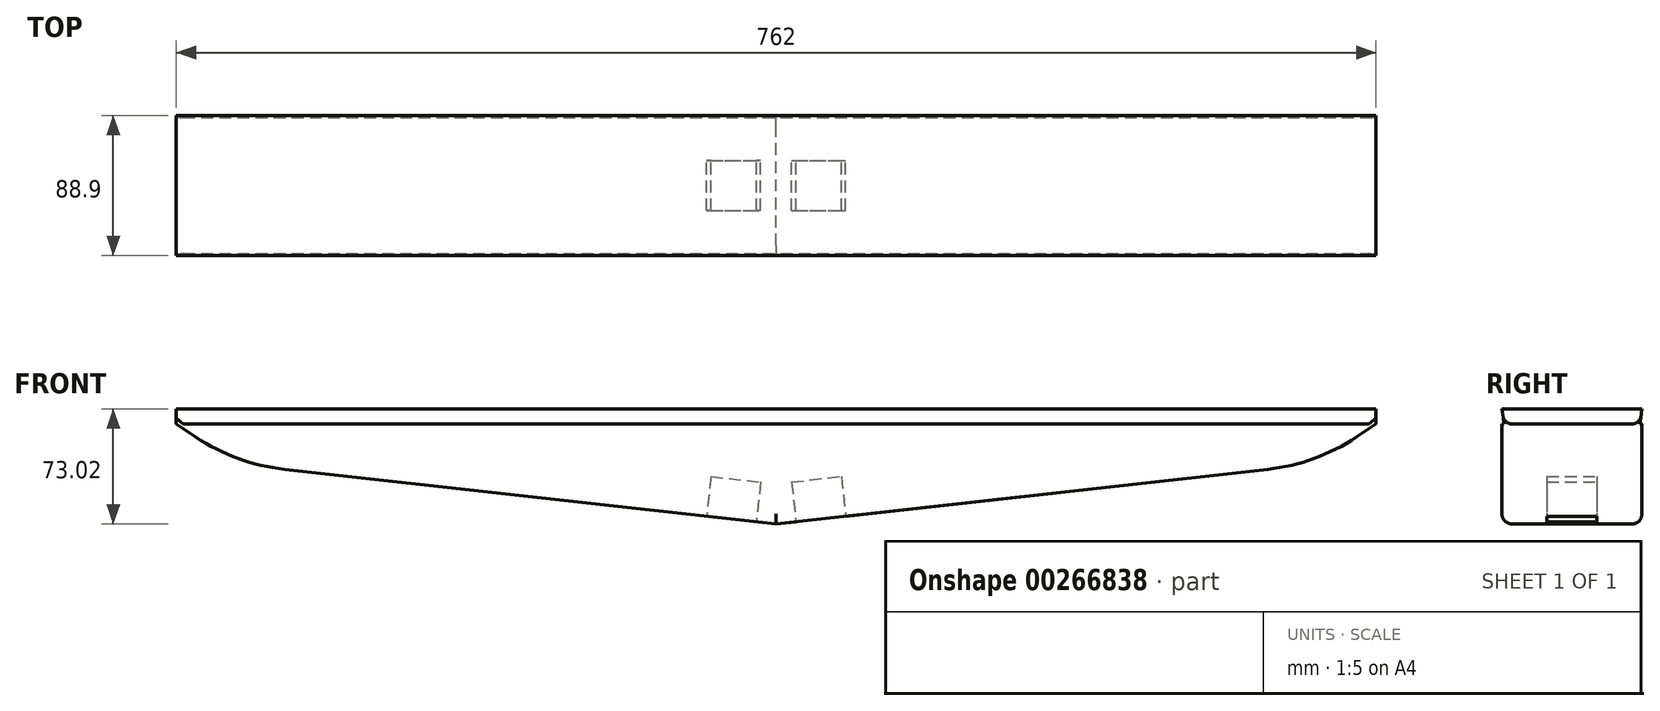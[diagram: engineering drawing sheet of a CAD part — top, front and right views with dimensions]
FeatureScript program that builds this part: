
annotation { "Feature Type Name" : "Feature", "Feature Type Description" : "" }
export const myFeature = defineFeature(function(context is Context, id is Id, definition is map)
    precondition{}
    {
        {
            var Q0;
            Q0=qCreatedBy(makeId("Front.planeOp"),FACE);
            var sketch = newSketch(context, id + "F0", { "sketchPlane" : qUnion([Q0])});
            skLineSegment(sketch, "E0", {"start": v(-380.27, 108.93) * mm, "end": v(381.73, 108.93) * mm});
            skLineSegment(sketch, "E1", {"start": v(312.91, 80.12) * mm, "end": v(0.73, 45.43) * mm});
            skLineSegment(sketch, "E2", {"start": v(0.73, 45.43) * mm, "end": v(-311.46, 80.12) * mm});
            skLineSegment(sketch, "E3", {"start": v(-367.88, 100.67) * mm, "end": v(-380.27, 108.93) * mm});
            skPoint(sketch, "E4", {"position": v(343.63, 83.53) * mm});
            skPoint(sketch, "E5.orphan", {"position": v(381.73, 87.76) * mm});
            skLineSegment(sketch, "E6", {"start": v(381.73, 108.93) * mm, "end": v(369.34, 100.67) * mm});
            skLineSegment(sketch, "E7.top", {"start": v(-380.27, 118.45) * mm, "end": v(381.73, 118.45) * mm});
            skLineSegment(sketch, "E7.left", {"start": v(-380.27, 108.93) * mm, "end": v(-380.27, 118.45) * mm});
            skLineSegment(sketch, "E7.right", {"start": v(381.73, 108.93) * mm, "end": v(381.73, 118.45) * mm});
            skLineSegment(sketch, "E8", {"start": v(31.55, 48.85) * mm, "end": v(35.36, 14.56) * mm});
            skPoint(sketch, "E9.visualSharp", {"position": v(-342.17, 83.53) * mm});
            skArc(sketch, "E9.filletArc", {"start": v(-367.88, 100.67) * mm, "mid": v(-340.9, 87.01) * mm, "end": v(-311.46, 80.12) * mm});
            skArc(sketch, "E10.filletArc", {"start": v(312.91, 80.12) * mm, "mid": v(342.36, 87.01) * mm, "end": v(369.34, 100.67) * mm});
            skSolve(sketch);
        }
        {
            var Q0;
            Q0 = qSketchRegion(id + "F0", true);
            var Q1;
            Q1 = qSketchRegion(id + "F2", true);
            extrude(context, id + "F1", {"entities" : qUnion([Q0, Q1]), "endBound" : BoundingType.SYMMETRIC, "depth" : 88.9 * mm});
        }
        {
            var Q0;
            Q0=makeQuery(id+"F1.opExtrude","SWEPT_FACE",FACE,{"disambiguationData":[OSD([sQuery(id+"F0.wireOp",EDGE,"E2")])]});
            var sketch = newSketch(context, id + "F2", { "sketchPlane" : qUnion([Q0])});
            skLineSegment(sketch, "E11.bottom", {"start": v(-48.75, 15.88) * mm, "end": v(-17, 15.88) * mm});
            skLineSegment(sketch, "E11.top", {"start": v(-48.75, -15.88) * mm, "end": v(-17, -15.88) * mm});
            skLineSegment(sketch, "E11.left", {"start": v(-48.75, 15.88) * mm, "end": v(-48.75, -15.88) * mm});
            skLineSegment(sketch, "E11.right", {"start": v(-17, 15.88) * mm, "end": v(-17, -15.88) * mm});
            skPoint(sketch, "E11.middle", {"position": v(-32.87, 0) * mm});
            skSolve(sketch);
        }
        {
            var Q0;
            Q0=makeQuery(id+"F2.imprint","IMPRINT",FACE,{"disambiguationData":[TD([[makeQuery(id+"F2.imprint","IMPRINT",EDGE,{"derivedFrom":sQuery(id+"F2.wireOp",EDGE,"E11.bottom")}),-1.0]])]});
            extrude(context, id + "F3", {"entities" : qUnion([Q0]), "operationType" : NewBodyOperationType.REMOVE, "oppositeDirection" : true, "depth" : 25.4 * mm});
        }
        {
            var Q0;
            Q0=makeQuery(id+"F1.opExtrude","SWEPT_FACE",FACE,{"disambiguationData":[OSD([sQuery(id+"F0.wireOp",EDGE,"E1")])]});
            var sketch = newSketch(context, id + "F4", { "sketchPlane" : qUnion([Q0])});
            skLineSegment(sketch, "E12.bottom", {"start": v(18.44, 15.88) * mm, "end": v(50.19, 15.88) * mm});
            skLineSegment(sketch, "E12.top", {"start": v(18.44, -15.87) * mm, "end": v(50.19, -15.87) * mm});
            skLineSegment(sketch, "E12.left", {"start": v(18.44, 15.88) * mm, "end": v(18.44, -15.87) * mm});
            skLineSegment(sketch, "E12.right", {"start": v(50.19, 15.88) * mm, "end": v(50.19, -15.87) * mm});
            skPoint(sketch, "E12.middle", {"position": v(34.31, 0) * mm});
            skSolve(sketch);
        }
        {
            var Q0;
            Q0=makeQuery(id+"F4.imprint","IMPRINT",FACE,{"disambiguationData":[TD([[makeQuery(id+"F4.imprint","IMPRINT",EDGE,{"derivedFrom":sQuery(id+"F4.wireOp",EDGE,"E12.bottom")}),-1.0]])]});
            extrude(context, id + "F5", {"entities" : qUnion([Q0]), "operationType" : NewBodyOperationType.REMOVE, "oppositeDirection" : true, "depth" : 25.4 * mm});
        }
        {
            var Q0;
            Q0=makeQuery(id+"F1.opExtrude","SWEPT_FACE",FACE,{"disambiguationData":[OSD([sQuery(id+"F0.wireOp",EDGE,"E7.right")])]});
            var sketch = newSketch(context, id + "F6", { "sketchPlane" : qUnion([Q0])});
            skLineSegment(sketch, "E13", {"start": v(-44.45, 118.45) * mm, "end": v(-43.11, 108.93) * mm});
            skLineSegment(sketch, "E14", {"start": v(-43.11, 108.93) * mm, "end": v(-44.45, 108.93) * mm});
            skLineSegment(sketch, "E15", {"start": v(-44.45, 108.93) * mm, "end": v(-44.45, 118.45) * mm});
            skLineSegment(sketch, "E16", {"start": v(44.45, 118.45) * mm, "end": v(43.11, 108.93) * mm});
            skLineSegment(sketch, "E17", {"start": v(43.11, 108.93) * mm, "end": v(44.45, 108.93) * mm});
            skLineSegment(sketch, "E18", {"start": v(44.45, 108.93) * mm, "end": v(44.45, 118.45) * mm});
            skSolve(sketch);
        }
        {
            var Q0;
            Q0=makeQuery(id+"F6.imprint","IMPRINT",FACE,{"disambiguationData":[TD([[makeQuery(id+"F6.imprint","IMPRINT",EDGE,{"derivedFrom":sQuery(id+"F6.wireOp",EDGE,"E13")}),-1.0]])]});
            extrude(context, id + "F7", {"entities" : qUnion([Q0]), "operationType" : NewBodyOperationType.REMOVE, "endBound" : BoundingType.THROUGH_ALL, "oppositeDirection" : true, "depth" : 25.4 * mm});
        }
        {
            var Q0;
            Q0=makeQuery(id+"F1.opExtrude","SWEPT_FACE",FACE,{"disambiguationData":[OSD([sQuery(id+"F0.wireOp",EDGE,"E7.right")])]});
            var sketch = newSketch(context, id + "F8", { "sketchPlane" : qUnion([Q0])});
            skLineSegment(sketch, "E19", {"start": v(44.45, 118.45) * mm, "end": v(43.11, 108.93) * mm});
            skLineSegment(sketch, "E20", {"start": v(43.11, 108.93) * mm, "end": v(44.45, 108.93) * mm});
            skLineSegment(sketch, "E21", {"start": v(44.45, 108.93) * mm, "end": v(44.45, 118.45) * mm});
            skSolve(sketch);
        }
        {
            var Q0;
            Q0=makeQuery(id+"F8.imprint","IMPRINT",FACE,{"disambiguationData":[TD([[makeQuery(id+"F8.imprint","IMPRINT",EDGE,{"derivedFrom":sQuery(id+"F8.wireOp",EDGE,"E19")}),1.0]])]});
            extrude(context, id + "F9", {"entities" : qUnion([Q0]), "operationType" : NewBodyOperationType.REMOVE, "endBound" : BoundingType.THROUGH_ALL, "oppositeDirection" : true, "depth" : 25.4 * mm});
        }
        {
            var Q0;
            Q0=makeQuery(id+"F1.opExtrude","CAP_EDGE",EDGE,{"disambiguationData":[OSD([sQuery(id+"F0.wireOp",EDGE,"E2")])],"isStart":false});
            var Q1;
            Q1=makeQuery(id+"F1.opExtrude","CAP_EDGE",EDGE,{"disambiguationData":[OSD([sQuery(id+"F0.wireOp",EDGE,"E1")])],"isStart":false});
            var Q2;
            Q2=makeQuery(id+"F1.opExtrude","CAP_EDGE",EDGE,{"disambiguationData":[OSD([sQuery(id+"F0.wireOp",EDGE,"E1")])],"isStart":true});
            var Q3;
            Q3=makeQuery(id+"F1.opExtrude","CAP_EDGE",EDGE,{"disambiguationData":[OSD([sQuery(id+"F0.wireOp",EDGE,"E2")])],"isStart":true});
            fillet(context, id + "F10", {"entities" : qUnion([Q0, Q1, Q2, Q3]), "radius" : 6.35 * mm, "tangentPropagation" : true, "allowEdgeOverflow" : false});
        }
    });
